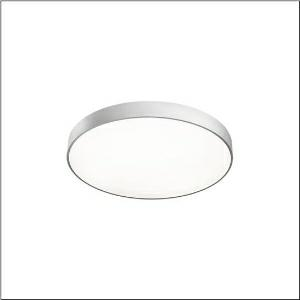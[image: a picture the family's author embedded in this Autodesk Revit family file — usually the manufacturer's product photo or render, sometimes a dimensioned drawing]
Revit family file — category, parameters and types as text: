
# Revit family: round_21_m_51mr36gm8321s
name_source: partatom
category: Lighting Fixtures
units: mm (PartAtom-declared; Revit-internal decimal feet)

## family parameters
Cut with Voids When Loaded = No
Host = Face
Light Source = No
Part Type = Normal
Room Calculation Point = No
Round Connector Dimension = Use Diameter
Shared = No

## types (1)
- --- (1 x LED, 8610 lm, 62.3 W, 3000K)
    Apparent Load = 62 VA
    CIE Flux Codes = 49 80 96 85 100
    Color Rendering = 80
    Color Temperature = 3000K
    Default Elevation = 1800 mm
    Description = Round 21 M, wall and ceiling luminaire, primary optical cover: cover, of PMMA, opal, light emission: direct/indirect distribution, primary light characteristic: symmetric, installation type: suspended mounting, surface-mounted, LED, rated luminous flux: 8.600lm, luminous efficacy: 138lm/W, light colour: 830, colour temperature: 3000K, control gear: ON/OFF Multilumen, with terminal, 3-pole, mains connection: 230V, AC, 50/60Hz, rated input power: 62.3W, housing, of aluminium, coated, silver, diameter: 600mm, height: 62mm, protection rating (complete): IP40, insulation class (complete): insulation class I (protective earthing), certification: CE, impact resistance: IK04, permissible operating ambient temperature: -10..+35°C, packaging unit: 1 piece
    Height = 87 mm
    Lamp = 1 x LED
    Lamp Light Flux = 8610 lm
    Lamp Power = 62.3 W
    Lamp count = 1
    Length = 600 mm
    Luminous efficacy = 138 lm/W
    Manufacturer = Siteco
    ModVariant = No
    Model = 51MR36GM8321S
    Mounting Place = Ceiling
    Mounting Type = Surface mounted
    Number of Poles = 1
    OnlyDefault = Yes
    Power Factor = 1
    Product Name = Round 21 M
    Product group = wall and ceiling luminaire
    ProductGroupID = 304
    Protection Class = Protection class I
    Protection Degree = IP 40
    RLX_Detail_Level = 1
    RLX_Emergency_Light_Flux = 0 lm
    RLX_Emergency_Type = 0
    RLX_Emergency_Type_DB = No
    RlxData = <blob elided: 17917 chars, md5=006dceb4>
    Socket = socket
    Standby Power = 0 W
    System Light Flux = 8610 lm
    System Power = 62 W
    Type Comments = factory setting: luminous flux: 100 % | (ON | ON | ON | ON) | 700 mA
    Type Image = l_1258303.jpg
    URL = http://relux.com
    VarID = @adj_032986
    Voltage = 0 V
    Weight = 0.00 kg
    Width = 0 mm  [stored 0 ft]

note: [stored X ft] marks values corroborated as IEEE doubles in the binary element streams (Revit-internal decimal feet)

## geometry (parser evidence)
native form markers: Blend x4, Sweep x14
no freeform markers — native parametric forms only
